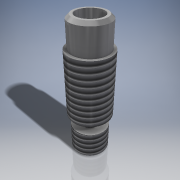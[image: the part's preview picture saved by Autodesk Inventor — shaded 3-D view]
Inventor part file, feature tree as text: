
AUTODESK INVENTOR PART (.ipt)
format: ipt  version: 2019 (Build 230136000, 136)  size: 157,184 bytes
history: native  units: mm
features: other x3, chamfer x3, sketch x3, extrude x2
ambient origin geometry x8: Origin, YZ Plane, XZ Plane, XY Plane, X Axis, Y Axis, Z Axis, Center Point
bodies: Solide1 (feature_tree)
feature tree (11):
  other  "Révolution1"
  extrude  "Extrusion1"  Depth=3.0mm
  extrude  "Extrusion2"  Depth=4.5mm
  chamfer  "Chanfrein1"  Distance=0.5mm
  chamfer  "Chanfrein2"  Distance=10.5mm
  chamfer  "Chanfrein3"  Distance=22.1mm
  other  "Filetage1"
  other  "Filetage2"
  sketch  "Esquisse1"
  sketch  "Esquisse2"
  sketch  "Esquisse3"
